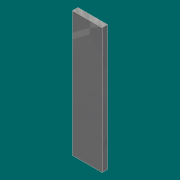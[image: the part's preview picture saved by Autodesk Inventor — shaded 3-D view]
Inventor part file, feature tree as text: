
AUTODESK INVENTOR PART (.ipt)
format: ipt  version: 2017 (Build 210142000, 142)  size: 72,704 bytes
history: native  units: in
note: dims shown in document units (in); Inventor stores cm internally (conversion verified against a paired STEP export)
features: extrude x1, sketch x1
ambient origin geometry x8: Origin, YZ Plane, XZ Plane, XY Plane, X Axis, Y Axis, Z Axis, Center Point
bodies: Solid1 (feature_tree)
feature tree (2):
  extrude  "Extrusion1"  Depth=2.75in
  sketch  "Sketch1"  dims[d0=0.65in d1=2.75in d2=0.12in d3=0.0in]
